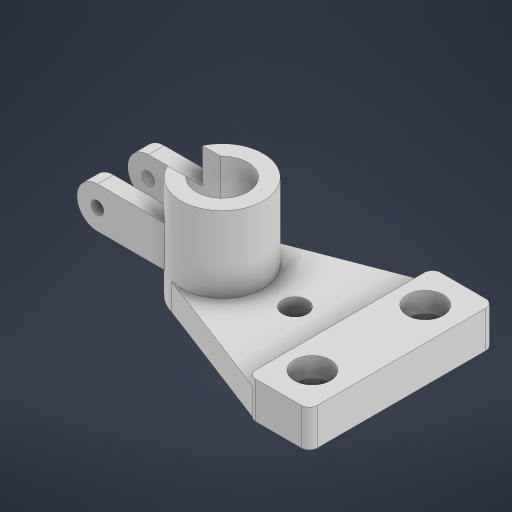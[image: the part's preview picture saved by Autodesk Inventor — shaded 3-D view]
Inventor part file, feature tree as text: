
AUTODESK INVENTOR PART (.ipt)
format: ipt  version: 2023 (Build 270158000, 158)  size: 318,464 bytes
history: native  units: mm
features: sketch x10, extrude x5, other x3, hole x3
ambient origin geometry x8: Origin, YZ Plane, XZ Plane, XY Plane, X Axis, Y Axis, Z Axis, Center Point
bodies: Body1 (feature_tree)
feature tree (21):
  other  "Bryła1"
  extrude  "Wyciągnięcie proste1"  Depth=60.0mm
  extrude  "Wyciągnięcie proste2"  Depth=180.0mm
  extrude  "Wyciągnięcie proste3"  Depth=8.0mm
  extrude  "Wyciągnięcie proste4"  Depth=3.665191mm
  extrude  "Wyciągnięcie proste5"  Depth=3.665191mm
  sketch  "Szkic6"
  sketch  "Szkic7"
  hole  "Otwór1"  [1 undecoded]
  hole  "Otwór2"  [1 undecoded]
  sketch  "Szkic9"
  hole  "Otwór3"  [1 undecoded]
  other  "Zaokrąglenie pełne1"
  other  "Zaokrąglenie pełne2"
  sketch  "Szkic1"
  sketch  "Szkic2"
  sketch  "Szkic3"
  sketch  "Szkic4"
  sketch  "Szkic5"
  sketch  "Szkic8"
  sketch  "Szkic10"
note: 3 required parameter values undecoded (feature->parameter linkage not recoverable at this tier; creation-order binding heuristic only, values carry confidence <= 0.55)
